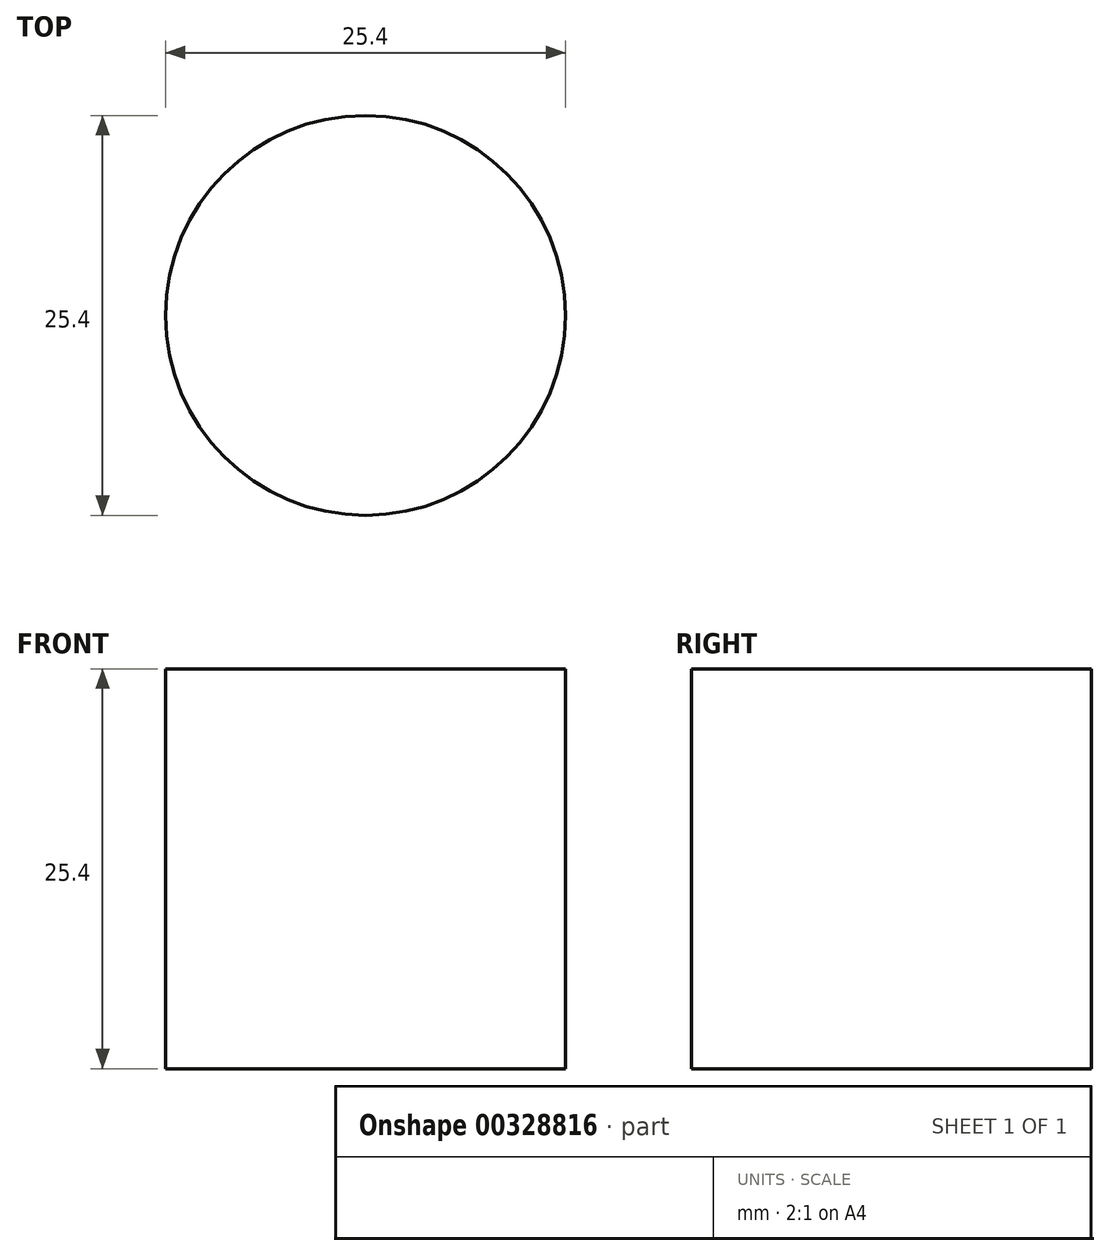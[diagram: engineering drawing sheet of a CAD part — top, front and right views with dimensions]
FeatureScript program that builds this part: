
annotation { "Feature Type Name" : "Feature", "Feature Type Description" : "" }
export const myFeature = defineFeature(function(context is Context, id is Id, definition is map)
    precondition{}
    {
        {
            var Q0;
            Q0=qCreatedBy(makeId("Top.planeOp"),FACE);
            var sketch = newSketch(context, id + "F0", { "sketchPlane" : qUnion([Q0])});
            skCircle(sketch, "E0", {"center": v(0, 0) * mm, "radius": 12.7 * mm});
            skSolve(sketch);
        }
        {
            var Q0;
            Q0=sQuery(id+"F0.wireOp",EDGE,"E0");
            extrude(context, id + "F1", {"bodyType" : ToolBodyType.SURFACE, "operationType" : NewBodyOperationType.ADD, "surfaceEntities" : qUnion([Q0]), "depth" : 25.4 * mm});
        }
    });
